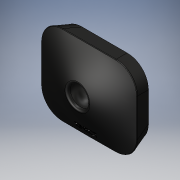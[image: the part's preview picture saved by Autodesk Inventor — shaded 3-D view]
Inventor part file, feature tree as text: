
AUTODESK INVENTOR PART (.ipt)
format: ipt  version: 2018 (Build 220112000, 112)  size: 491,520 bytes
history: native  units: in
note: dims shown in document units (in); Inventor stores cm internally (conversion verified against a paired STEP export)
features: fillet x1
ambient origin geometry x8: Origin, YZ Plane, XZ Plane, XY Plane, X Axis, Y Axis, Z Axis, Center Point
bodies: Solid1 (feature_tree)
feature tree (1):
  fillet  "Fillet3"  [1 undecoded]
note: 1 required parameter value undecoded (feature->parameter linkage not recoverable at this tier; creation-order binding heuristic only, values carry confidence <= 0.55)
